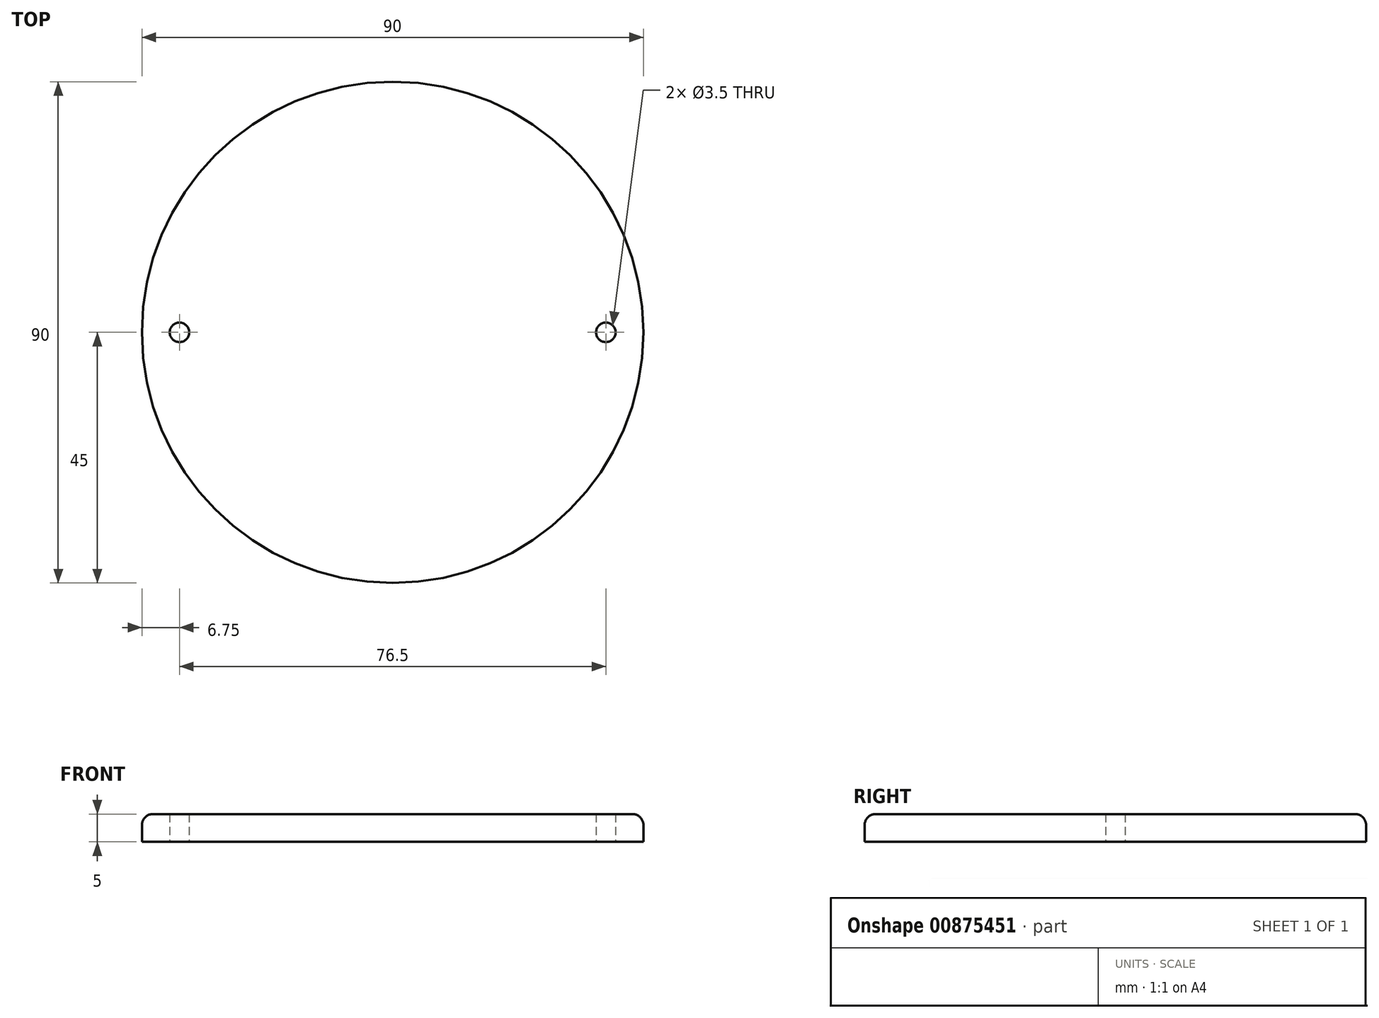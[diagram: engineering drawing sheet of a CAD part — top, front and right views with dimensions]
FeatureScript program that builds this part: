
annotation { "Feature Type Name" : "Feature", "Feature Type Description" : "" }
export const myFeature = defineFeature(function(context is Context, id is Id, definition is map)
    precondition{}
    {
        {
            var Q0;
            Q0=qCreatedBy(makeId("Top.planeOp"),FACE);
            var sketch = newSketch(context, id + "F0", { "sketchPlane" : qUnion([Q0])});
            skCircle(sketch, "E0", {"center": v(0, 0) * mm, "radius": 45 * mm});
            skCircle(sketch, "E1", {"center": v(-38.25, 0) * mm, "radius": 1.75 * mm});
            skCircle(sketch, "E2.MirrorC", {"center": v(38.25, 0) * mm, "radius": 1.75 * mm});
            skSolve(sketch);
        }
        {
            var Q0;
            Q0=makeQuery(id+"F0.imprint","IMPRINT",FACE,{"disambiguationData":[TD([[makeQuery(id+"F0.imprint","IMPRINT",EDGE,{"derivedFrom":sQuery(id+"F0.wireOp",EDGE,"E0")}),1.0]])]});
            extrude(context, id + "F1", {"entities" : qUnion([Q0]), "depth" : 5 * mm, "offsetDistance" : 25 * mm});
        }
        {
            var Q0;
            Q0=makeQuery(id+"F1.opExtrude","CAP_EDGE",EDGE,{"disambiguationData":[OSD([sQuery(id+"F0.wireOp",EDGE,"E0")])],"isStart":false});
            fillet(context, id + "F2", {"entities" : qUnion([Q0]), "radius" : 2 * mm, "tangentPropagation" : true, "allowEdgeOverflow" : false});
        }
    });
